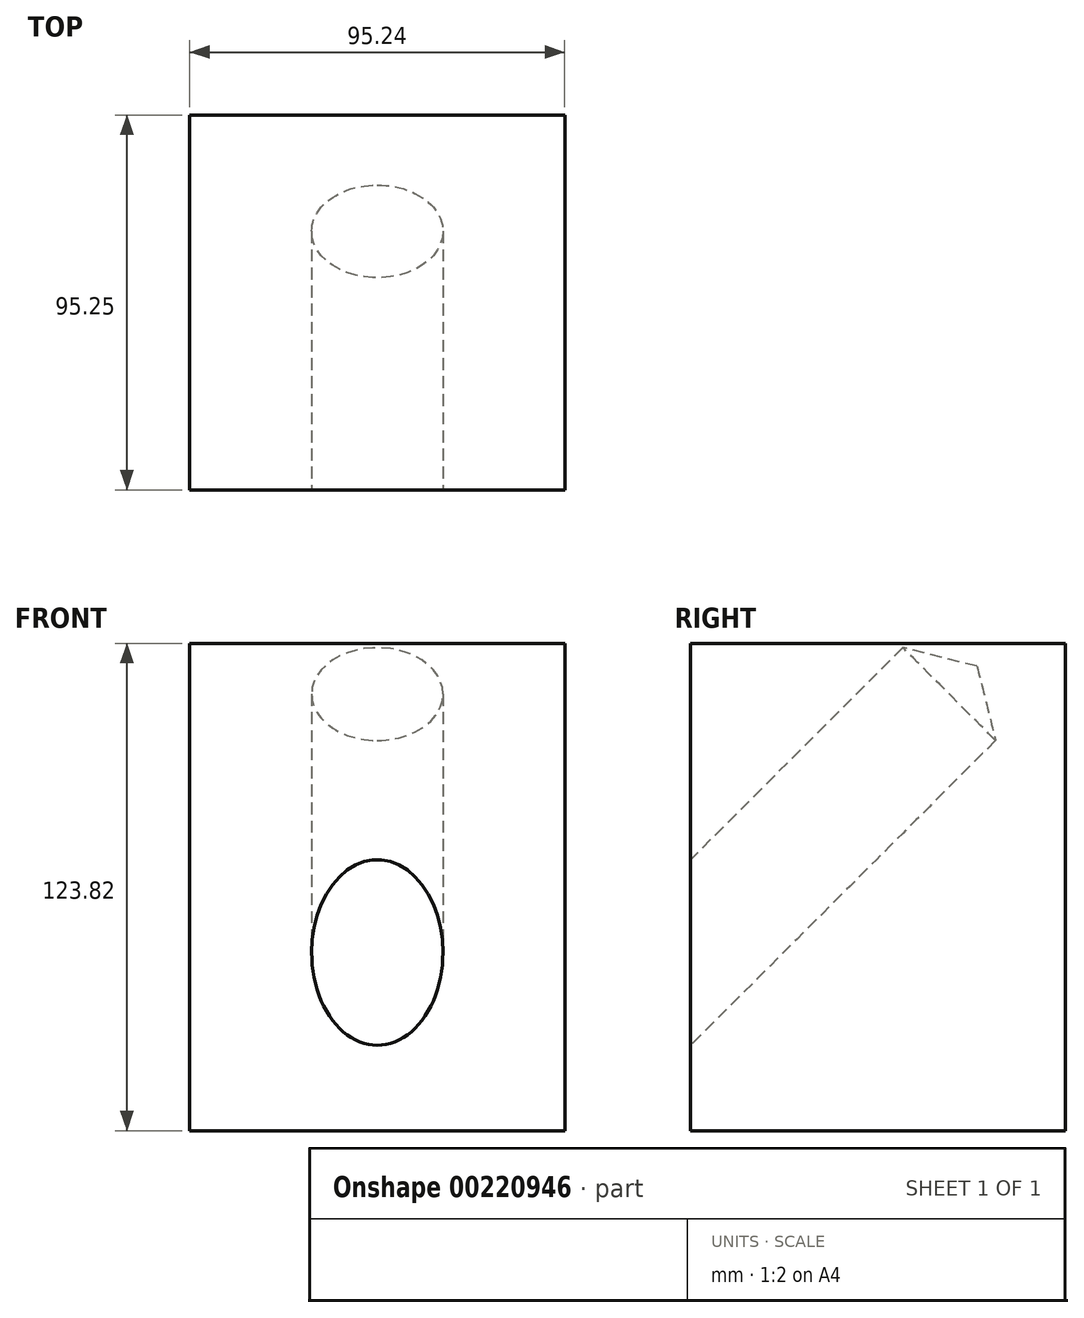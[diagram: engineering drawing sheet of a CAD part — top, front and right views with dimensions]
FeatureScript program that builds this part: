
annotation { "Feature Type Name" : "Feature", "Feature Type Description" : "" }
export const myFeature = defineFeature(function(context is Context, id is Id, definition is map)
    precondition{}
    {
        {
            var Q0;
            Q0=qCreatedBy(makeId("Front.planeOp"),FACE);
            var sketch = newSketch(context, id + "F0", { "sketchPlane" : qUnion([Q0])});
            skLineSegment(sketch, "E0.bottom", {"start": v(-47.63, 61.91) * mm, "end": v(47.62, 61.91) * mm});
            skLineSegment(sketch, "E0.top", {"start": v(-47.62, -61.91) * mm, "end": v(47.63, -61.91) * mm});
            skLineSegment(sketch, "E0.left", {"start": v(-47.63, 61.91) * mm, "end": v(-47.62, -61.91) * mm});
            skLineSegment(sketch, "E0.right", {"start": v(47.62, 61.91) * mm, "end": v(47.63, -61.91) * mm});
            skSolve(sketch);
        }
        {
            var Q0;
            Q0=makeQuery(id+"F0.imprint","IMPRINT",FACE,{"disambiguationData":[TD([[makeQuery(id+"F0.imprint","IMPRINT",EDGE,{"derivedFrom":sQuery(id+"F0.wireOp",EDGE,"E0.bottom")}),-1.0]])]});
            extrude(context, id + "F1", {"entities" : qUnion([Q0]), "depth" : 95.25 * mm});
        }
        {
            var Q0;
            Q0=makeQuery(id+"F1.opExtrude","CAP_FACE",FACE,{"disambiguationData":[OSD([sQuery(id+"F0.wireOp",EDGE,"E0.bottom"),sQuery(id+"F0.wireOp",EDGE,"E0.top"),sQuery(id+"F0.wireOp",EDGE,"E0.left"),sQuery(id+"F0.wireOp",EDGE,"E0.right")])],"isStart":false});
            var sketch = newSketch(context, id + "F2", { "sketchPlane" : qUnion([Q0])});
            skSolve(sketch);
        }
        {
            var Q0;
            Q0=makeQuery(id+"F2.imprint","IMPRINT",FACE,{"disambiguationData":[TD([[makeQuery(id+"F2.imprint","IMPRINT",EDGE,{"derivedFrom":makeQuery(id+"F1.opExtrude","CAP_EDGE",EDGE,{"disambiguationData":[OSD([sQuery(id+"F0.wireOp",EDGE,"E0.bottom")])],"isStart":false})}),-1.0]])]});
            var Q1;
            Q1=makeQuery(id+"F1.opExtrude","CAP_EDGE",EDGE,{"disambiguationData":[OSD([sQuery(id+"F0.wireOp",EDGE,"E0.top")])],"isStart":false});
            cPlane(context, id + "F3", {"entities" : qUnion([Q0, Q1]), "cplaneType" : CPlaneType.LINE_ANGLE, "offset" : 25.4 * mm, "angle" : 45 * degree, "width" : 152.4 * mm, "height" : 152.4 * mm});
        }
        {
            var Q0;
            Q0=qCreatedBy(id+"F3.planeOp",FACE);
            var sketch = newSketch(context, id + "F4", { "sketchPlane" : qUnion([Q0])});
            skCircle(sketch, "E1", {"center": v(0, 55.58) * mm, "radius": 16.67 * mm});
            skSolve(sketch);
        }
        {
            var Q0;
            Q0=sQuery(id+"F4.wireOp",VERTEX,"E1.center");
            var Q1;
            Q1=makeQuery(id+"F1.opExtrude","SWEPT_BODY",BODY,{"disambiguationData":[OSD([sQuery(id+"F0.wireOp",EDGE,"E0.bottom"),sQuery(id+"F0.wireOp",EDGE,"E0.top"),sQuery(id+"F0.wireOp",EDGE,"E0.left"),sQuery(id+"F0.wireOp",EDGE,"E0.right")])]});
            hole(context, id + "F5", {"style" : HoleStyle.SIMPLE, "endStyle" : HoleEndStyle.BLIND, "oppositeDirection" : true, "holeDiameter" : 33.34 * mm, "holeDepth" : 76.2 * mm, "locations" : qUnion([Q0]), "scope" : qUnion([Q1])});
        }
    });
